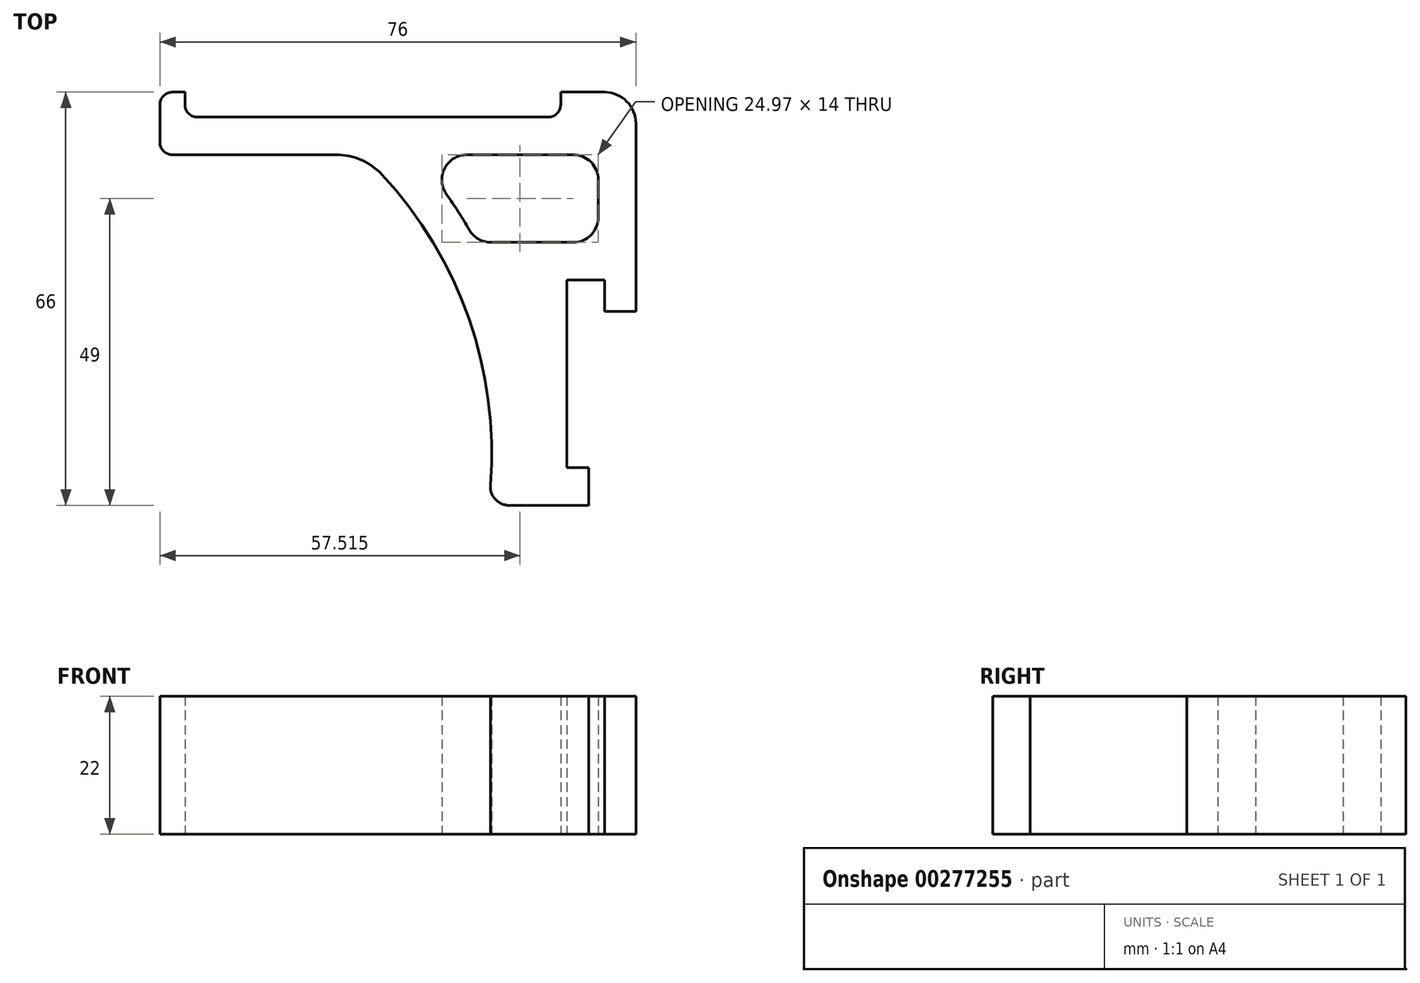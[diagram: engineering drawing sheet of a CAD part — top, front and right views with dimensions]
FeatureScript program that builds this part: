
annotation { "Feature Type Name" : "Feature", "Feature Type Description" : "" }
export const myFeature = defineFeature(function(context is Context, id is Id, definition is map)
    precondition{}
    {
        {
            var Q0;
            Q0=qCreatedBy(makeId("Top.planeOp"),FACE);
            var sketch = newSketch(context, id + "F0", { "sketchPlane" : qUnion([Q0])});
            skLineSegment(sketch, "E0", {"start": v(-23.56, -56) * mm, "end": v(-7.5, -56) * mm});
            skLineSegment(sketch, "E1", {"start": v(-7.5, -50) * mm, "end": v(-11, -50) * mm});
            skLineSegment(sketch, "E2", {"start": v(-11, -50) * mm, "end": v(-11, -20) * mm});
            skLineSegment(sketch, "E3", {"start": v(-11, -20) * mm, "end": v(-5, -20) * mm});
            skLineSegment(sketch, "E4", {"start": v(-5, -20) * mm, "end": v(-5, -25) * mm});
            skLineSegment(sketch, "E5", {"start": v(-5, -25) * mm, "end": v(0, -25) * mm});
            skLineSegment(sketch, "E6", {"start": v(0, -25) * mm, "end": v(0, 0) * mm});
            skPoint(sketch, "E7.orphan", {"position": v(0, -56) * mm});
            skLineSegment(sketch, "E8", {"start": v(-43.7, 0) * mm, "end": v(-76, 0) * mm});
            skLineSegment(sketch, "E9", {"start": v(0, 0) * mm, "end": v(0, 10) * mm});
            skLineSegment(sketch, "E10", {"start": v(0, 10) * mm, "end": v(-12, 10) * mm});
            skLineSegment(sketch, "E11", {"start": v(-12, 6) * mm, "end": v(-72, 6) * mm});
            skLineSegment(sketch, "E12", {"start": v(-72, 6) * mm, "end": v(-72, 10) * mm});
            skLineSegment(sketch, "E13", {"start": v(-72, 10) * mm, "end": v(-76, 10) * mm});
            skLineSegment(sketch, "E14", {"start": v(-76, 10) * mm, "end": v(-76, 0) * mm});
            skPoint(sketch, "E15.orphan", {"position": v(-11, 8.92) * mm});
            skLineSegment(sketch, "E16", {"start": v(-12, 10) * mm, "end": v(-12, 6) * mm});
            skArc(sketch, "E17", {"start": v(-23.56, -56) * mm, "mid": v(-26.88, -25.57) * mm, "end": v(-43.7, 0) * mm});
            skArc(sketch, "E18.0", {"start": v(-25.47, -14) * mm, "mid": v(-29.97, -6.7) * mm, "end": v(-35.3, 0) * mm});
            skLineSegment(sketch, "E18.1", {"start": v(-25.47, -14) * mm, "end": v(-6, -14) * mm});
            skLineSegment(sketch, "E18.2", {"start": v(-6, -14) * mm, "end": v(-6, 0) * mm});
            skLineSegment(sketch, "E18.3", {"start": v(-6, 0) * mm, "end": v(-35.3, 0) * mm});
            skLineSegment(sketch, "E19", {"start": v(-7.5, -56) * mm, "end": v(-7.5, -50) * mm});
            skSolve(sketch);
        }
        {
            var Q0;
            Q0=makeQuery(id+"F0.imprint","IMPRINT",FACE,{"disambiguationData":[TD([[makeQuery(id+"F0.imprint","IMPRINT",EDGE,{"derivedFrom":sQuery(id+"F0.wireOp",EDGE,"E0")}),1.0]])]});
            extrude(context, id + "F1", {"entities" : qUnion([Q0]), "depth" : 22 * mm});
        }
        {
            var Q0;
            Q0=makeQuery(id+"F1.opExtrude","SWEPT_EDGE",EDGE,{"disambiguationData":[OSD([sQuery(id+"F0.wireOp",EDGE,"E8"),sQuery(id+"F0.wireOp",EDGE,"E17")])]});
            fillet(context, id + "F2", {"entities" : qUnion([Q0]), "radius" : 10 * mm, "tangentPropagation" : true, "allowEdgeOverflow" : false});
        }
        {
            var Q0;
            Q0=makeQuery(id+"F1.opExtrude","SWEPT_EDGE",EDGE,{"disambiguationData":[OSD([sQuery(id+"F0.wireOp",EDGE,"E0"),sQuery(id+"F0.wireOp",EDGE,"E17")])]});
            fillet(context, id + "F3", {"entities" : qUnion([Q0]), "radius" : 3 * mm, "tangentPropagation" : true, "allowEdgeOverflow" : false});
        }
        {
            var Q0;
            Q0=makeQuery(id+"F1.opExtrude","SWEPT_EDGE",EDGE,{"disambiguationData":[OSD([sQuery(id+"F0.wireOp",EDGE,"E18.0"),sQuery(id+"F0.wireOp",EDGE,"E18.3")])]});
            var Q1;
            Q1=makeQuery(id+"F1.opExtrude","SWEPT_EDGE",EDGE,{"disambiguationData":[OSD([sQuery(id+"F0.wireOp",EDGE,"E18.2"),sQuery(id+"F0.wireOp",EDGE,"E18.3")])]});
            var Q2;
            Q2=makeQuery(id+"F1.opExtrude","SWEPT_EDGE",EDGE,{"disambiguationData":[OSD([sQuery(id+"F0.wireOp",EDGE,"E18.0"),sQuery(id+"F0.wireOp",EDGE,"E18.1")])]});
            var Q3;
            Q3=makeQuery(id+"F1.opExtrude","SWEPT_EDGE",EDGE,{"disambiguationData":[OSD([sQuery(id+"F0.wireOp",EDGE,"E18.1"),sQuery(id+"F0.wireOp",EDGE,"E18.2")])]});
            fillet(context, id + "F4", {"entities" : qUnion([Q0, Q1, Q2, Q3]), "radius" : 4 * mm, "tangentPropagation" : true, "allowEdgeOverflow" : false});
        }
        {
            var Q0;
            Q0=makeQuery(id+"F1.opExtrude","SWEPT_EDGE",EDGE,{"disambiguationData":[OSD([sQuery(id+"F0.wireOp",EDGE,"E9"),sQuery(id+"F0.wireOp",EDGE,"E10")])]});
            fillet(context, id + "F5", {"entities" : qUnion([Q0]), "radius" : 5 * mm, "tangentPropagation" : true, "allowEdgeOverflow" : false});
        }
        {
            var Q0;
            Q0=makeQuery(id+"F1.opExtrude","SWEPT_EDGE",EDGE,{"disambiguationData":[OSD([sQuery(id+"F0.wireOp",EDGE,"E11"),sQuery(id+"F0.wireOp",EDGE,"E16")])]});
            var Q1;
            Q1=makeQuery(id+"F1.opExtrude","SWEPT_EDGE",EDGE,{"disambiguationData":[OSD([sQuery(id+"F0.wireOp",EDGE,"E11"),sQuery(id+"F0.wireOp",EDGE,"E12")])]});
            fillet(context, id + "F6", {"entities" : qUnion([Q0, Q1]), "radius" : 2 * mm, "tangentPropagation" : true, "allowEdgeOverflow" : false});
        }
        {
            var Q0;
            Q0=makeQuery(id+"F1.opExtrude","SWEPT_EDGE",EDGE,{"disambiguationData":[OSD([sQuery(id+"F0.wireOp",EDGE,"E13"),sQuery(id+"F0.wireOp",EDGE,"E14")])]});
            var Q1;
            Q1=makeQuery(id+"F1.opExtrude","SWEPT_EDGE",EDGE,{"disambiguationData":[OSD([sQuery(id+"F0.wireOp",EDGE,"E8"),sQuery(id+"F0.wireOp",EDGE,"E14")])]});
            fillet(context, id + "F7", {"entities" : qUnion([Q0, Q1]), "radius" : 2 * mm, "tangentPropagation" : true, "allowEdgeOverflow" : false});
        }
    });
